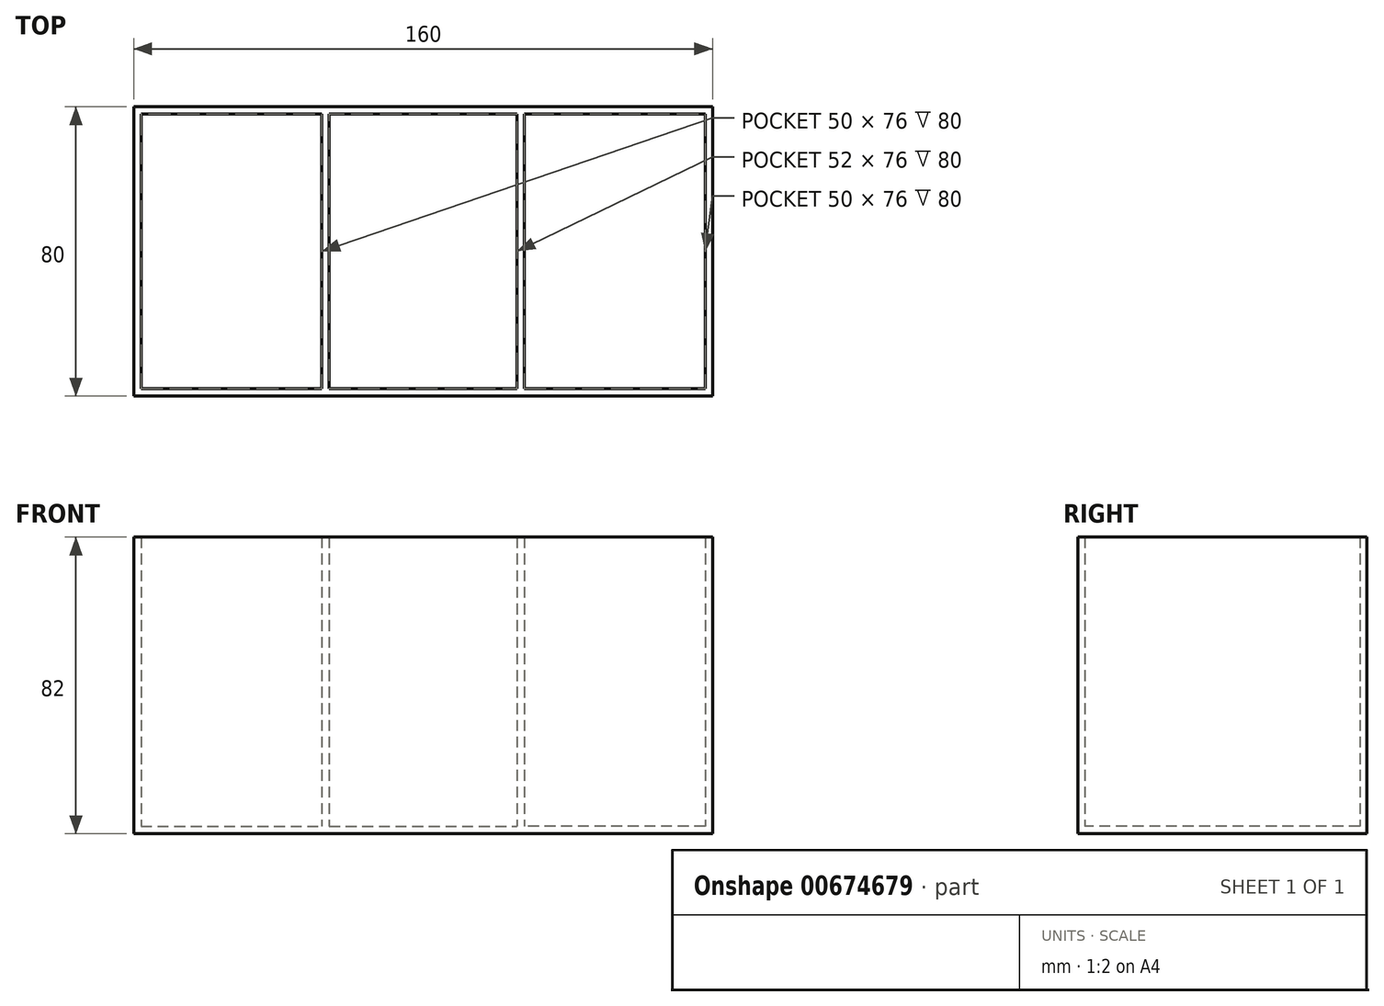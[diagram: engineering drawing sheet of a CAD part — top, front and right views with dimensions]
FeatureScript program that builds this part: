
annotation { "Feature Type Name" : "Feature", "Feature Type Description" : "" }
export const myFeature = defineFeature(function(context is Context, id is Id, definition is map)
    precondition{}
    {
        {
            var Q0;
            Q0=qCreatedBy(makeId("Top.planeOp"),FACE);
            var sketch = newSketch(context, id + "F0", { "sketchPlane" : qUnion([Q0])});
            skLineSegment(sketch, "E0.bottom", {"start": v(0, 0) * mm, "end": v(160, 0) * mm});
            skLineSegment(sketch, "E0.top", {"start": v(0, 80) * mm, "end": v(160, 80) * mm});
            skLineSegment(sketch, "E0.left", {"start": v(0, 0) * mm, "end": v(0, 80) * mm});
            skLineSegment(sketch, "E0.right", {"start": v(160, 0) * mm, "end": v(160, 80) * mm});
            skSolve(sketch);
        }
        {
            var Q0;
            Q0 = qSketchRegion(id + "F0", true);
            extrude(context, id + "F1", {"entities" : qUnion([Q0]), "depth" : 2 * mm, "offsetDistance" : 25 * mm});
        }
        {
            var Q0;
            Q0=makeQuery(id+"F1.opExtrude","CAP_FACE",FACE,{"disambiguationData":[OSD([sQuery(id+"F0.wireOp",EDGE,"E0.bottom"),sQuery(id+"F0.wireOp",EDGE,"E0.top"),sQuery(id+"F0.wireOp",EDGE,"E0.left"),sQuery(id+"F0.wireOp",EDGE,"E0.right")])],"isStart":false});
            var sketch = newSketch(context, id + "F2", { "sketchPlane" : qUnion([Q0])});
            skLineSegment(sketch, "E1.bottom", {"start": v(0, 0) * mm, "end": v(54, 0) * mm});
            skLineSegment(sketch, "E1.top", {"start": v(0, 80) * mm, "end": v(54, 80) * mm});
            skLineSegment(sketch, "E1.left", {"start": v(0, 0) * mm, "end": v(0, 80) * mm});
            skLineSegment(sketch, "E1.right", {"start": v(54, 0) * mm, "end": v(54, 80) * mm});
            skLineSegment(sketch, "E2.0", {"start": v(158, 78) * mm, "end": v(2, 78) * mm});
            skLineSegment(sketch, "E2.1", {"start": v(158, 2) * mm, "end": v(158, 78) * mm});
            skLineSegment(sketch, "E2.2", {"start": v(2, 2) * mm, "end": v(158, 2) * mm});
            skLineSegment(sketch, "E2.3", {"start": v(2, 78) * mm, "end": v(2, 2) * mm});
            skLineSegment(sketch, "E3", {"start": v(52, 78) * mm, "end": v(52, 2) * mm});
            skLineSegment(sketch, "E4.bottom", {"start": v(160, 0) * mm, "end": v(106, 0) * mm});
            skLineSegment(sketch, "E4.top", {"start": v(160, 80) * mm, "end": v(106, 80) * mm});
            skLineSegment(sketch, "E4.left", {"start": v(160, 0) * mm, "end": v(160, 80) * mm});
            skLineSegment(sketch, "E4.right", {"start": v(106, 0) * mm, "end": v(106, 80) * mm});
            skLineSegment(sketch, "E5", {"start": v(108, 78) * mm, "end": v(108, 2) * mm});
            skSolve(sketch);
        }
        {
            var Q0;
            {var subQ5=sQuery(id+"F2.wireOp",EDGE,"E3");Q0=makeQuery(id+"F2.imprint","IMPRINT",FACE,{"disambiguationData":[TD([[makeQuery(id+"F2.imprint","IMPRINT",EDGE,{"derivedFrom":subQ5}),1.0]])]});}
            var Q1;
            {var subQ0=sQuery(id+"F2.wireOp",EDGE,"E5");Q1=makeQuery(id+"F2.imprint","IMPRINT",FACE,{"disambiguationData":[TD([[makeQuery(id+"F2.imprint","IMPRINT",EDGE,{"derivedFrom":subQ0}),-1.0]])]});}
            var Q2;
            {var subQ1=sQuery(id+"F2.wireOp",EDGE,"E1.bottom");Q2=makeQuery(id+"F2.imprint","IMPRINT",FACE,{"disambiguationData":[TD([[makeQuery(id+"F2.imprint","IMPRINT",EDGE,{"derivedFrom":subQ1}),1.0]])]});}
            var Q3;
            {var subQ8=sQuery(id+"F2.wireOp",EDGE,"E2.1");Q3=makeQuery(id+"F2.imprint","IMPRINT",FACE,{"disambiguationData":[TD([[makeQuery(id+"F2.imprint","IMPRINT",EDGE,{"derivedFrom":subQ8}),-1.0]])]});}
            var Q4;
            {var subQ0=sQuery(id+"F2.wireOp",EDGE,"E1.right");var subQ3=sQuery(id+"F2.wireOp",EDGE,"E2.2");var subQ4=makeQuery(id+"F2.imprint","INTERSECT",VERTEX,{"derivedFrom":[subQ0,subQ3]});Q4=makeQuery(id+"F2.imprint","IMPRINT",FACE,{"disambiguationData":[TD([[makeQuery(id+"F2.imprint","IMPRINT",EDGE,{"disambiguationData":[TD([[subQ4,-1.0]])],"derivedFrom":subQ3}),-1.0]])]});}
            var Q5;
            {var subQ0=sQuery(id+"F2.wireOp",EDGE,"E1.right");var subQ3=sQuery(id+"F2.wireOp",EDGE,"E2.0");var subQ4=makeQuery(id+"F2.imprint","INTERSECT",VERTEX,{"derivedFrom":[subQ0,subQ3]});Q5=makeQuery(id+"F2.imprint","IMPRINT",FACE,{"disambiguationData":[TD([[makeQuery(id+"F2.imprint","IMPRINT",EDGE,{"disambiguationData":[TD([[subQ4,1.0]])],"derivedFrom":subQ3}),-1.0]])]});}
            extrude(context, id + "F3", {"entities" : qUnion([Q0, Q1, Q2, Q3, Q4, Q5]), "operationType" : NewBodyOperationType.ADD, "depth" : 80 * mm, "offsetDistance" : 25 * mm});
        }
    });
